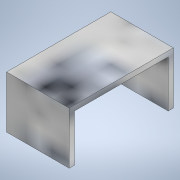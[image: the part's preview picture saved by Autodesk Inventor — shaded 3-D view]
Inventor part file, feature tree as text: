
AUTODESK INVENTOR PART (.ipt)
format: ipt  version: 2022 (Build 260153000, 153)  size: 138,240 bytes
history: native  units: in
note: dims shown in document units (in); Inventor stores cm internally (conversion verified against a paired STEP export)
features: extrude x1, sketch x1
ambient origin geometry x8: Origin, YZ Plane, XZ Plane, XY Plane, X Axis, Y Axis, Z Axis, Center Point
bodies: Solid1 (feature_tree)
feature tree (2):
  extrude  "Extrusion1"  Depth=0.05in
  sketch  "Sketch1"  dims[d0=1.0in d1=0.05in d2=0.5in d3=0.6in d4=0.0in]
